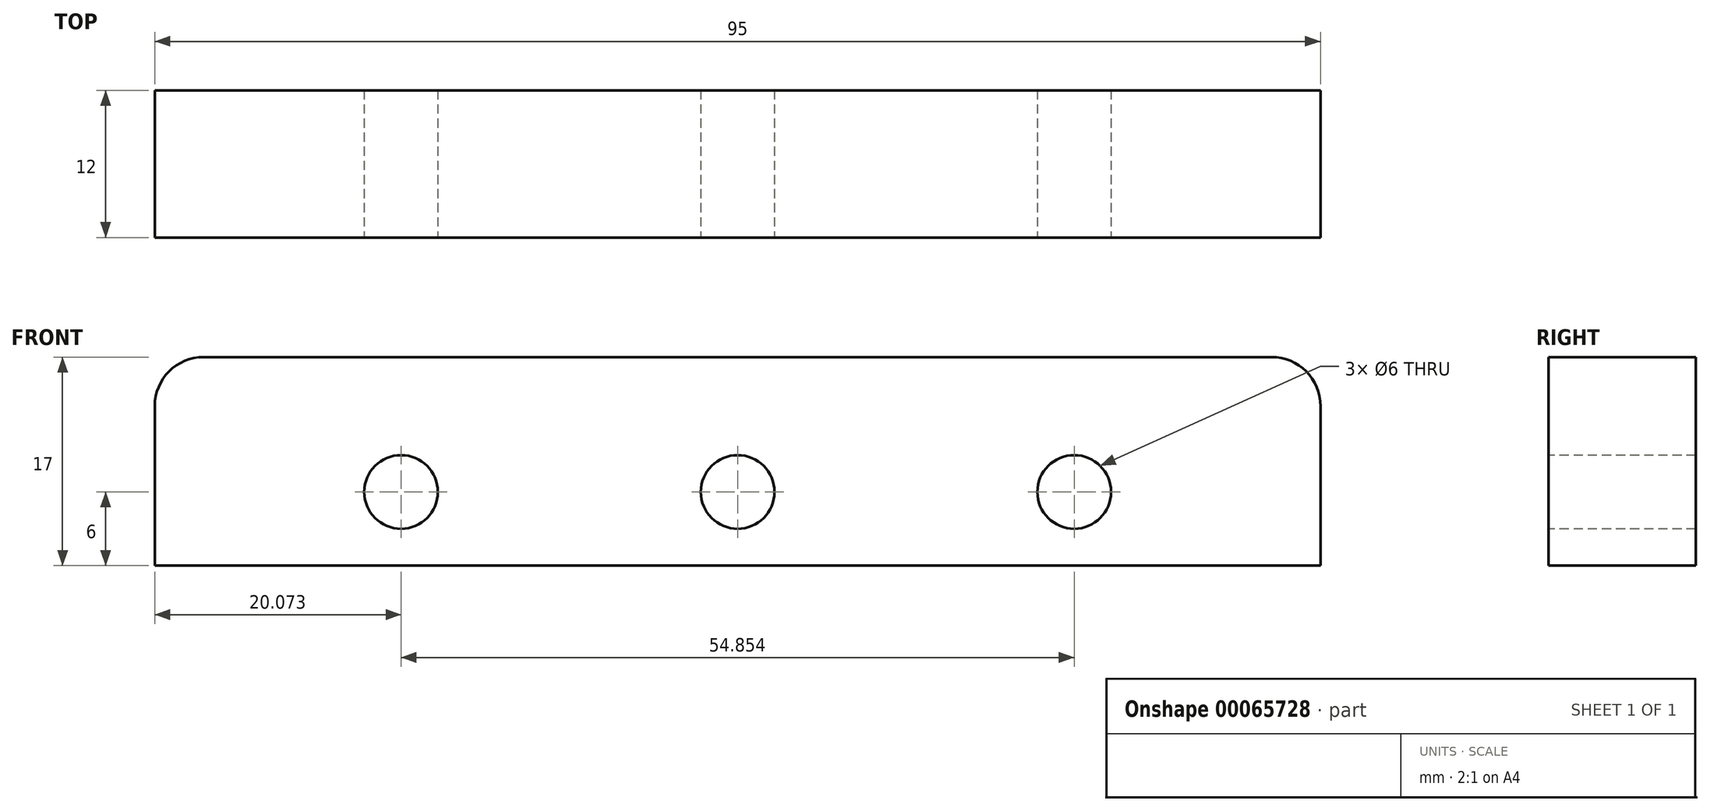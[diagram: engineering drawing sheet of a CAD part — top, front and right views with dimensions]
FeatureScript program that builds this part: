
annotation { "Feature Type Name" : "Feature", "Feature Type Description" : "" }
export const myFeature = defineFeature(function(context is Context, id is Id, definition is map)
    precondition{}
    {
        {
            var Q0;
            Q0=qCreatedBy(makeId("Top.planeOp"),FACE);
            var sketch = newSketch(context, id + "F0", { "sketchPlane" : qUnion([Q0])});
            skPoint(sketch, "E0.rect.middle", {"position": v(0, 0) * mm});
            skLineSegment(sketch, "E1", {"start": v(0, 0) * mm, "end": v(0, 2) * mm});
            skLineSegment(sketch, "E2", {"start": v(0, 2) * mm, "end": v(12, 2) * mm, "construction": true});
            skCircle(sketch, "E3", {"center": v(12, 2) * mm, "radius": 3 * mm});
            skCircle(sketch, "E4", {"center": v(12, 2) * mm, "radius": 6 * mm});
            skCircle(sketch, "E5.MirrorC", {"center": v(-12, 2) * mm, "radius": 3 * mm});
            skCircle(sketch, "E6.MirrorC", {"center": v(-12, 2) * mm, "radius": 6 * mm});
            skLineSegment(sketch, "E7.rect.left", {"start": v(-37.5, -4) * mm, "end": v(-37.5, 8) * mm});
            skLineSegment(sketch, "E7.rect.right", {"start": v(37.5, -4) * mm, "end": v(37.5, 8) * mm});
            skPoint(sketch, "E7.rect.middle", {"position": v(0, 2) * mm});
            skLineSegment(sketch, "E8", {"start": v(37.5, -4) * mm, "end": v(-37.5, -4) * mm});
            skLineSegment(sketch, "E9", {"start": v(37.5, 8) * mm, "end": v(-37.5, 8) * mm});
            skLineSegment(sketch, "E10.bottom", {"start": v(-37.5, 8) * mm, "end": v(-47.5, 8) * mm});
            skLineSegment(sketch, "E10.top", {"start": v(-37.5, -4) * mm, "end": v(-47.5, -4) * mm});
            skLineSegment(sketch, "E10.left", {"start": v(-37.5, 8) * mm, "end": v(-37.5, -4) * mm});
            skLineSegment(sketch, "E10.right", {"start": v(-47.5, 8) * mm, "end": v(-47.5, -4) * mm});
            skLineSegment(sketch, "E11.bottom", {"start": v(37.5, 8) * mm, "end": v(47.5, 8) * mm});
            skLineSegment(sketch, "E11.top", {"start": v(37.5, -4) * mm, "end": v(47.5, -4) * mm});
            skLineSegment(sketch, "E11.left", {"start": v(37.5, 8) * mm, "end": v(37.5, -4) * mm});
            skLineSegment(sketch, "E11.right", {"start": v(47.5, 8) * mm, "end": v(47.5, -4) * mm});
            skSolve(sketch);
        }
        {
            var Q0;
            {var subQ5=sQuery(id+"F0.wireOp",EDGE,"E7.rect.left");Q0=makeQuery(id+"F0.imprint","IMPRINT",FACE,{"disambiguationData":[TD([[makeQuery(id+"F0.imprint","IMPRINT",EDGE,{"derivedFrom":subQ5}),-1.0]])]});}
            var Q1;
            Q1=makeQuery(id+"F0.imprint","IMPRINT",FACE,{"disambiguationData":[TD([[makeQuery(id+"F0.imprint","IMPRINT",EDGE,{"derivedFrom":sQuery(id+"F0.wireOp",EDGE,"E5.MirrorC")}),1.0]])]});
            var Q2;
            Q2=makeQuery(id+"F0.imprint","IMPRINT",FACE,{"disambiguationData":[TD([[makeQuery(id+"F0.imprint","IMPRINT",EDGE,{"derivedFrom":sQuery(id+"F0.wireOp",EDGE,"E5.MirrorC")}),-1.0]])]});
            var Q3;
            {var subQ0=sQuery(id+"F0.wireOp",EDGE,"E8");var subQ1=sQuery(id+"F0.wireOp",EDGE,"E4");var subQ2=makeQuery(id+"F0.imprint","INTERSECT",VERTEX,{"derivedFrom":[subQ1,subQ0]});Q3=makeQuery(id+"F0.imprint","IMPRINT",FACE,{"disambiguationData":[TD([[makeQuery(id+"F0.imprint","IMPRINT",EDGE,{"disambiguationData":[TD([[subQ2,1.0]])],"derivedFrom":subQ1}),-1.0]])]});}
            var Q4;
            Q4=makeQuery(id+"F0.imprint","IMPRINT",FACE,{"disambiguationData":[TD([[makeQuery(id+"F0.imprint","IMPRINT",EDGE,{"derivedFrom":sQuery(id+"F0.wireOp",EDGE,"E3")}),-1.0]])]});
            var Q5;
            Q5=makeQuery(id+"F0.imprint","IMPRINT",FACE,{"disambiguationData":[TD([[makeQuery(id+"F0.imprint","IMPRINT",EDGE,{"derivedFrom":sQuery(id+"F0.wireOp",EDGE,"E3")}),1.0]])]});
            var Q6;
            {var subQ5=sQuery(id+"F0.wireOp",EDGE,"E7.rect.right");Q6=makeQuery(id+"F0.imprint","IMPRINT",FACE,{"disambiguationData":[TD([[makeQuery(id+"F0.imprint","IMPRINT",EDGE,{"derivedFrom":subQ5}),1.0]])]});}
            var Q7;
            Q7=makeQuery(id+"F0.imprint","IMPRINT",FACE,{"disambiguationData":[TD([[makeQuery(id+"F0.imprint","IMPRINT",EDGE,{"derivedFrom":sQuery(id+"F0.wireOp",EDGE,"E10.bottom")}),1.0]])]});
            var Q8;
            {var subQ5=sQuery(id+"F0.wireOp",EDGE,"E10.left");Q8=makeQuery(id+"F0.imprint","IMPRINT",FACE,{"disambiguationData":[TD([[makeQuery(id+"F0.imprint","IMPRINT",EDGE,{"derivedFrom":subQ5}),1.0]])]});}
            var Q9;
            {var subQ5=sQuery(id+"F0.wireOp",EDGE,"E11.left");Q9=makeQuery(id+"F0.imprint","IMPRINT",FACE,{"disambiguationData":[TD([[makeQuery(id+"F0.imprint","IMPRINT",EDGE,{"derivedFrom":subQ5}),-1.0]])]});}
            var Q10;
            Q10=makeQuery(id+"F0.imprint","IMPRINT",FACE,{"disambiguationData":[TD([[makeQuery(id+"F0.imprint","IMPRINT",EDGE,{"derivedFrom":sQuery(id+"F0.wireOp",EDGE,"E11.bottom")}),-1.0]])]});
            extrude(context, id + "F1", {"entities" : qUnion([Q0, Q1, Q2, Q3, Q4, Q5, Q6, Q7, Q8, Q9, Q10]), "depth" : 17 * mm});
        }
        {
            var Q0;
            Q0=qCreatedBy(makeId("Front.planeOp"),FACE);
            var sketch = newSketch(context, id + "F2", { "sketchPlane" : qUnion([Q0])});
            skLineSegment(sketch, "E12", {"start": v(0, 0) * mm, "end": v(0, 12) * mm});
            skLineSegment(sketch, "E13", {"start": v(0, 6) * mm, "end": v(-27.43, 6) * mm, "construction": true});
            skCircle(sketch, "E14", {"center": v(-27.43, 6) * mm, "radius": 3 * mm});
            skCircle(sketch, "E15.MirrorC", {"center": v(27.43, 6) * mm, "radius": 3 * mm});
            skCircle(sketch, "E16", {"center": v(0, 6) * mm, "radius": 3 * mm});
            skSolve(sketch);
        }
        {
            var Q0;
            Q0 = qSketchRegion(id + "F2", true);
            extrude(context, id + "F3", {"entities" : qUnion([Q0]), "operationType" : NewBodyOperationType.REMOVE, "oppositeDirection" : true, "depth" : 25 * mm, "symmetric" : true});
        }
        {
            var Q0;
            Q0=makeQuery(id+"F1.opExtrude","CAP_EDGE",EDGE,{"disambiguationData":[OSD([sQuery(id+"F0.wireOp",EDGE,"E10.right")])],"isStart":false});
            var Q1;
            Q1=makeQuery(id+"F1.opExtrude","CAP_EDGE",EDGE,{"disambiguationData":[OSD([sQuery(id+"F0.wireOp",EDGE,"E11.right")])],"isStart":false});
            fillet(context, id + "F4", {"entities" : qUnion([Q0, Q1]), "radius" : 4 * mm, "tangentPropagation" : true, "allowEdgeOverflow" : false});
        }
    });
